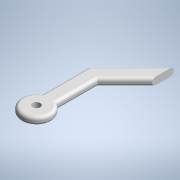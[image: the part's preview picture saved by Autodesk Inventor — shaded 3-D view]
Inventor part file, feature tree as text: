
AUTODESK INVENTOR PART (.ipt)
format: ipt  version: 2022 (Build 260153000, 153)  size: 142,336 bytes
history: native  units: mm (DEFAULTED — no unit token found)
features: extrude x1, fillet x1, sketch x1
ambient origin geometry x8: Origin, YZ Plane, XZ Plane, XY Plane, X Axis, Y Axis, Z Axis, Center Point
bodies: Solid1 (feature_tree)
feature tree (3):
  extrude  "Extrusion1"  TaperAngle=135.0deg  [1 undecoded]
  fillet  "Fillet1"  Radius=5.0mm
  sketch  "Sketch1"  dims[d2=20.0mm d8=135.0deg d11=5.0mm d12=0.0mm d13=2.0mm d14=23.284271mm]
note: 1 required parameter value undecoded (feature->parameter linkage not recoverable at this tier; creation-order binding heuristic only, values carry confidence <= 0.55)
